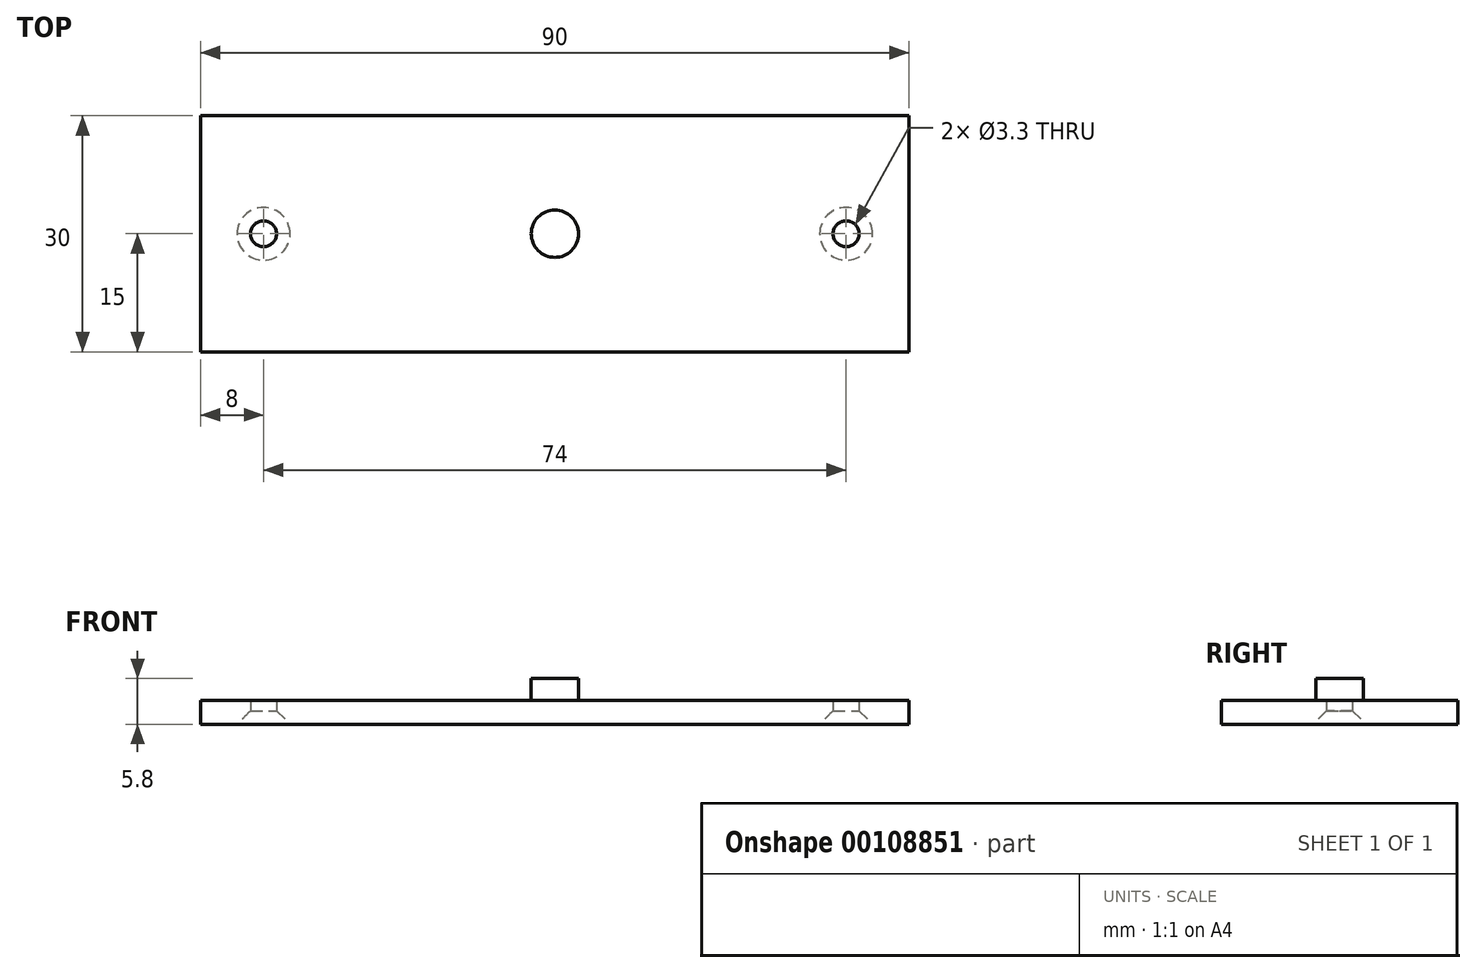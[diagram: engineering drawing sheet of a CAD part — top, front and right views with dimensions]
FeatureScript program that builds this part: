
annotation { "Feature Type Name" : "Feature", "Feature Type Description" : "" }
export const myFeature = defineFeature(function(context is Context, id is Id, definition is map)
    precondition{}
    {
        {
            var Q0;
            Q0=qCreatedBy(makeId("Top.planeOp"),FACE);
            var sketch = newSketch(context, id + "F0", { "sketchPlane" : qUnion([Q0])});
            skLineSegment(sketch, "E0", {"start": v(-51.73, 0) * mm, "end": v(57.01, 0) * mm, "construction": true});
            skLineSegment(sketch, "E1", {"start": v(0, -25.7) * mm, "end": v(0, 37.07) * mm, "construction": true});
            skLineSegment(sketch, "E2.bottom", {"start": v(-45, 0) * mm, "end": v(45, 0) * mm});
            skLineSegment(sketch, "E2.top", {"start": v(-45, 15) * mm, "end": v(45, 15) * mm});
            skLineSegment(sketch, "E2.left", {"start": v(-45, 0) * mm, "end": v(-45, 15) * mm});
            skLineSegment(sketch, "E2.right", {"start": v(45, 0) * mm, "end": v(45, 15) * mm});
            skLineSegment(sketch, "E3.MirrorCS", {"start": v(45, 0) * mm, "end": v(45, -15) * mm});
            skLineSegment(sketch, "E4.MirrorCS", {"start": v(-45, 0) * mm, "end": v(-45, -15) * mm});
            skLineSegment(sketch, "E5.MirrorCS", {"start": v(-45, -15) * mm, "end": v(45, -15) * mm});
            skLineSegment(sketch, "E6", {"start": v(-37, 8.85) * mm, "end": v(-37, -11.46) * mm, "construction": true});
            skLineSegment(sketch, "E7", {"start": v(37, 5.68) * mm, "end": v(37, -10.9) * mm, "construction": true});
            skCircle(sketch, "E8", {"center": v(0, 0) * mm, "radius": 3 * mm});
            skPoint(sketch, "E9", {"position": v(-37, 0) * mm});
            skPoint(sketch, "E9.positionSnap0", {"position": v(-37, -1.3) * mm});
            skPoint(sketch, "E10", {"position": v(37, 0) * mm});
            skSolve(sketch);
        }
        {
            var Q0;
            Q0 = qSketchRegion(id + "F0", true);
            extrude(context, id + "F1", {"entities" : qUnion([Q0]), "depth" : 3 * mm});
        }
        {
            var Q0;
            {var subQ0=sQuery(id+"F0.wireOp",EDGE,"E8");var subQ1=sQuery(id+"F0.wireOp",EDGE,"E2.bottom");var subQ2=makeQuery(id+"F0.imprint","INTERSECT",VERTEX,{"disambiguationData":[OD(0.0)],"derivedFrom":[subQ1,subQ0]});Q0=makeQuery(id+"F0.imprint","IMPRINT",FACE,{"disambiguationData":[TD([[makeQuery(id+"F0.imprint","IMPRINT",EDGE,{"disambiguationData":[TD([[subQ2,-1.0]])],"derivedFrom":subQ1}),1.0]])]});}
            var Q1;
            {var subQ0=sQuery(id+"F0.wireOp",EDGE,"E8");var subQ1=sQuery(id+"F0.wireOp",EDGE,"E2.bottom");var subQ2=makeQuery(id+"F0.imprint","INTERSECT",VERTEX,{"disambiguationData":[OD(0.0)],"derivedFrom":[subQ1,subQ0]});Q1=makeQuery(id+"F0.imprint","IMPRINT",FACE,{"disambiguationData":[TD([[makeQuery(id+"F0.imprint","IMPRINT",EDGE,{"disambiguationData":[TD([[subQ2,-1.0]])],"derivedFrom":subQ1}),-1.0]])]});}
            extrude(context, id + "F2", {"entities" : qUnion([Q0, Q1]), "operationType" : NewBodyOperationType.ADD, "depth" : 5.8 * mm});
        }
        {
            var Q0;
            Q0=sQuery(id+"F0.wireOp",VERTEX,"E9");
            var Q1;
            Q1=sQuery(id+"F0.wireOp",VERTEX,"E10");
            var Q2;
            Q2=makeQuery(id+"F1.opExtrude","SWEPT_BODY",BODY,{"disambiguationData":[OSD([sQuery(id+"F0.wireOp",EDGE,"E2.top"),sQuery(id+"F0.wireOp",EDGE,"E2.left"),sQuery(id+"F0.wireOp",EDGE,"E2.right"),sQuery(id+"F0.wireOp",EDGE,"E3.MirrorCS"),sQuery(id+"F0.wireOp",EDGE,"E4.MirrorCS"),sQuery(id+"F0.wireOp",EDGE,"E5.MirrorCS"),sQuery(id+"F0.wireOp",EDGE,"E8")])]});
            hole(context, id + "F3", {"style" : HoleStyle.C_SINK, "endStyle" : HoleEndStyle.THROUGH, "oppositeDirection" : true, "standardTappedOrClearance" : lookupTablePath({ "standard" : "ISO", "fit" : "Normal", "size" : "M3", "type" : "Clearance" }), "standardBlindInLast" : lookupTablePath({ "fit" : "Standard", "standard" : "ISO", "size" : "M3", "type" : "Clearance" }), "holeDiameter" : 3.3 * mm, "cSinkDiameter" : 6.72 * mm, "cSinkAngle" : 90 * degree, "startFromSketch" : true, "locations" : qUnion([Q0, Q1]), "scope" : qUnion([Q2]), "isTappedThrough" : true});
        }
    });
